# Revit family: Точечный двустворчатый зенитный фонарь (люк) M8CITY
name_source: partatom
category: Окна
revit_build: Autodesk Revit 2017 (Build: 20170118_1100(x64)
units: mm (PartAtom-declared; Revit-internal decimal feet)

## family parameters
Всегда вертикально = Нет
Общий = Нет
Основа = Крыша
При загрузке вырезать с полостями = Нет
Точка расчета площади = Нет

## types (1)
- Точечный двустворчатый зенитный фонарь (люк) M8CITY
    URL = www.m8city.by
    Высота = 573 мм
    Высота основания = 500 мм
    Длина = 2600 мм
    Длина проёма = 2600 мм
    Длина проёма ввод = 2600 мм
    Изготовитель = ООО Завод М8 Сити Про
    МПМ3 = Купол зенитного фонаря Ф st : МП молочный 3 мм
    МПМ4 = Купол зенитного фонаря Ф st : МП молочный 4 мм
    МПМ6 = Купол зенитного фонаря Ф st : МП молочный 3+3 мм
    МПМ7 = Купол зенитного фонаря Ф st : МП молочный 3+4 мм
    МПП3 = Купол зенитного фонаря Ф st : МП прозрачный 3 мм
    МПП4 = Купол зенитного фонаря Ф st : МП прозрачный 4 мм
    МПП6 = Купол зенитного фонаря Ф st : МП прозрачный 3+3 мм
    МПП7 = Купол зенитного фонаря Ф st : МП прозрачный 3+4 мм
    Описание = Точечный зенитный фонарь M8CITY с формованным куполом со стандартным обрамлением
    ПСМ16 = Купол зенитного фонаря П pro : ПС молочный 16 мм
    ПСМ20 = Купол зенитного фонаря П pro : ПС молочный 20 мм
    ПСП16 = Купол зенитного фонаря П pro : ПС прозрачный 16 мм
    ПСП20 = Купол зенитного фонаря П pro : ПС прозрачный 20 мм
    СП24 = Купол зенитного фонаря П pro : СП 24 мм
    СП26 = Купол зенитного фонаря П pro : СП 26 мм
    СПА25 = Купол зенитного фонаря П pro : Сендвич-панель 25 мм
    Установка привода = 1200 мм
    Ширина = 1700 мм
    Ширина проёма = 1700 мм
    Ширина проёма ввод = 1700 мм
